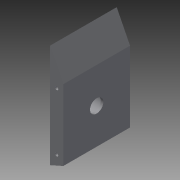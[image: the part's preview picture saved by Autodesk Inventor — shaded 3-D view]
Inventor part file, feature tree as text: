
AUTODESK INVENTOR PART (.ipt)
format: ipt  version: 2015 (Build 190159000, 159)  size: 94,720 bytes
history: native  units: mm
features: extrude x3, sketch x2
ambient origin geometry x8: Origin, YZ Plane, XZ Plane, XY Plane, X Axis, Y Axis, Z Axis, Center Point
bodies: Solid1 (feature_tree)
feature tree (5):
  extrude  "Extrusion1"  Depth=10.0mm
  sketch  "Sketch2"  dims[d2=4.444444mm d3=77.444444mm d8=2.5mm d9=2.5mm d10=50.0mm d11=0.0mm d12=25.0mm d13=15.0mm d14=10.0mm d15=0.0mm d16=10.0mm d17=2.0mm d18=0.0mm]
  extrude  "Extrusion2"  Depth=2.0mm
  extrude  "Extrusion3"  Depth=2.0mm
  sketch  "Sketch1"  dims[d0=10.0mm d1=53.0mm]
